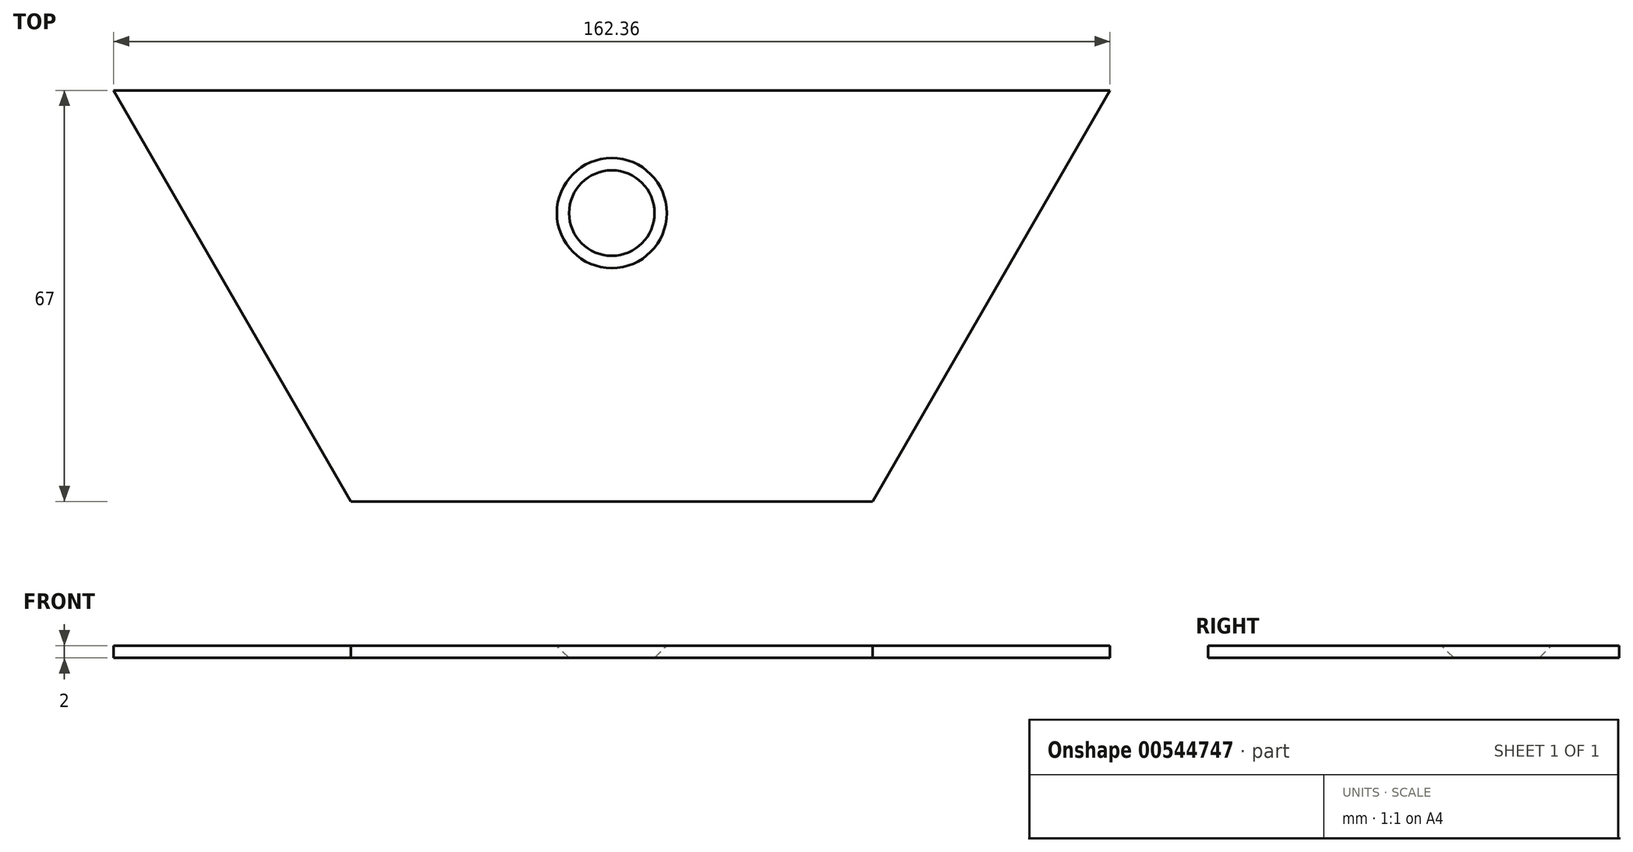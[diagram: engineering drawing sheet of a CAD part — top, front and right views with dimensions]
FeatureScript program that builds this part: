
annotation { "Feature Type Name" : "Feature", "Feature Type Description" : "" }
export const myFeature = defineFeature(function(context is Context, id is Id, definition is map)
    precondition{}
    {
        {
            var Q0;
            Q0=qCreatedBy(makeId("Top.planeOp"),FACE);
            var sketch = newSketch(context, id + "F0", { "sketchPlane" : qUnion([Q0])});
            skLineSegment(sketch, "E0", {"start": v(-42.5, 0) * mm, "end": v(42.5, 0) * mm});
            skLineSegment(sketch, "E1", {"start": v(42.5, 0) * mm, "end": v(81.18, 67) * mm});
            skLineSegment(sketch, "E2.MirrorCS", {"start": v(-42.5, 0) * mm, "end": v(-81.18, 67) * mm});
            skLineSegment(sketch, "E3", {"start": v(-81.18, 67) * mm, "end": v(81.18, 67) * mm});
            skPoint(sketch, "E4.orphan", {"position": v(-85, 73.61) * mm});
            skPoint(sketch, "E5.orphan", {"position": v(85, 73.61) * mm});
            skSolve(sketch);
        }
        {
            var Q0;
            Q0=makeQuery(id+"F0.imprint","IMPRINT",FACE,{"disambiguationData":[TD([[makeQuery(id+"F0.imprint","IMPRINT",EDGE,{"derivedFrom":sQuery(id+"F0.wireOp",EDGE,"E0")}),1.0]])]});
            extrude(context, id + "F1", {"entities" : qUnion([Q0]), "depth" : 2 * mm, "offsetDistance" : 25 * mm});
        }
        {
            var Q0;
            Q0=makeQuery(id+"F1.opExtrude","CAP_FACE",FACE,{"disambiguationData":[OSD([sQuery(id+"F0.wireOp",EDGE,"E0"),sQuery(id+"F0.wireOp",EDGE,"E1"),sQuery(id+"F0.wireOp",EDGE,"E2.MirrorCS"),sQuery(id+"F0.wireOp",EDGE,"E3")])],"isStart":false});
            var sketch = newSketch(context, id + "F2", { "sketchPlane" : qUnion([Q0])});
            skPoint(sketch, "E6", {"position": v(0, 47) * mm});
            skSolve(sketch);
        }
        {
            var Q0;
            Q0=sQuery(id+"F2.wireOp",VERTEX,"E6");
            var Q1;
            Q1=makeQuery(id+"F1.opExtrude","SWEPT_BODY",BODY,{"disambiguationData":[OSD([sQuery(id+"F0.wireOp",EDGE,"E0"),sQuery(id+"F0.wireOp",EDGE,"E1"),sQuery(id+"F0.wireOp",EDGE,"E2.MirrorCS"),sQuery(id+"F0.wireOp",EDGE,"E3")])]});
            hole(context, id + "F3", {"style" : HoleStyle.C_SINK, "endStyle" : HoleEndStyle.THROUGH, "standardTappedOrClearance" : lookupTablePath({ "standard" : "ISO", "fit" : "Normal", "size" : "M8", "type" : "Clearance" }), "standardBlindInLast" : lookupTablePath({ "fit" : "Standard", "standard" : "ISO", "size" : "M8", "type" : "Clearance" }), "holeDiameter" : 8.8 * mm, "cSinkDiameter" : 17.92 * mm, "cSinkAngle" : 90 * degree, "isTappedThrough" : true, "tappedDepth" : 12 * mm, "tapClearance" : 3, "locations" : qUnion([Q0]), "scope" : qUnion([Q1])});
        }
    });
